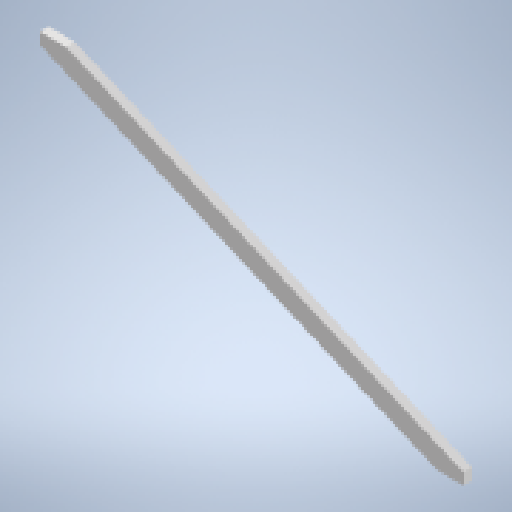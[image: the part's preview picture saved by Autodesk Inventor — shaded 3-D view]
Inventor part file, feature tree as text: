
AUTODESK INVENTOR PART (.ipt)
format: ipt  version: 2025.1 (Build 291241020, 241B)  size: 135,680 bytes
history: native  units: in
note: dims shown in document units (in); Inventor stores cm internally (conversion verified against a paired STEP export)
features: other x6, reference x4, extrude x1, sketch x1
ambient origin geometry x8: Origin, YZ Plane, XZ Plane, XY Plane, X Axis, Y Axis, Z Axis, Center Point
bodies: Solid1 (feature_tree)
feature tree (12):
  extrude  "Extrusion1"  [1 undecoded]
  sketch  "Sketch1"  dims[d2=1.5in d3=0.0in]
  reference  "Reference1"
  reference  "Reference2"
  reference  "Reference3"
  reference  "Reference4"
  other  "<userpath>\Documents\Tburn24\Assembly1.iam"
  other  "Assembly1.iam"
  other  "16'x2x4:1"
  other  "6'x4x4:19"
  other  "16'x4x4:2"
  other  "6'x4x4:15"
note: 1 required parameter value undecoded (feature->parameter linkage not recoverable at this tier; creation-order binding heuristic only, values carry confidence <= 0.55)
